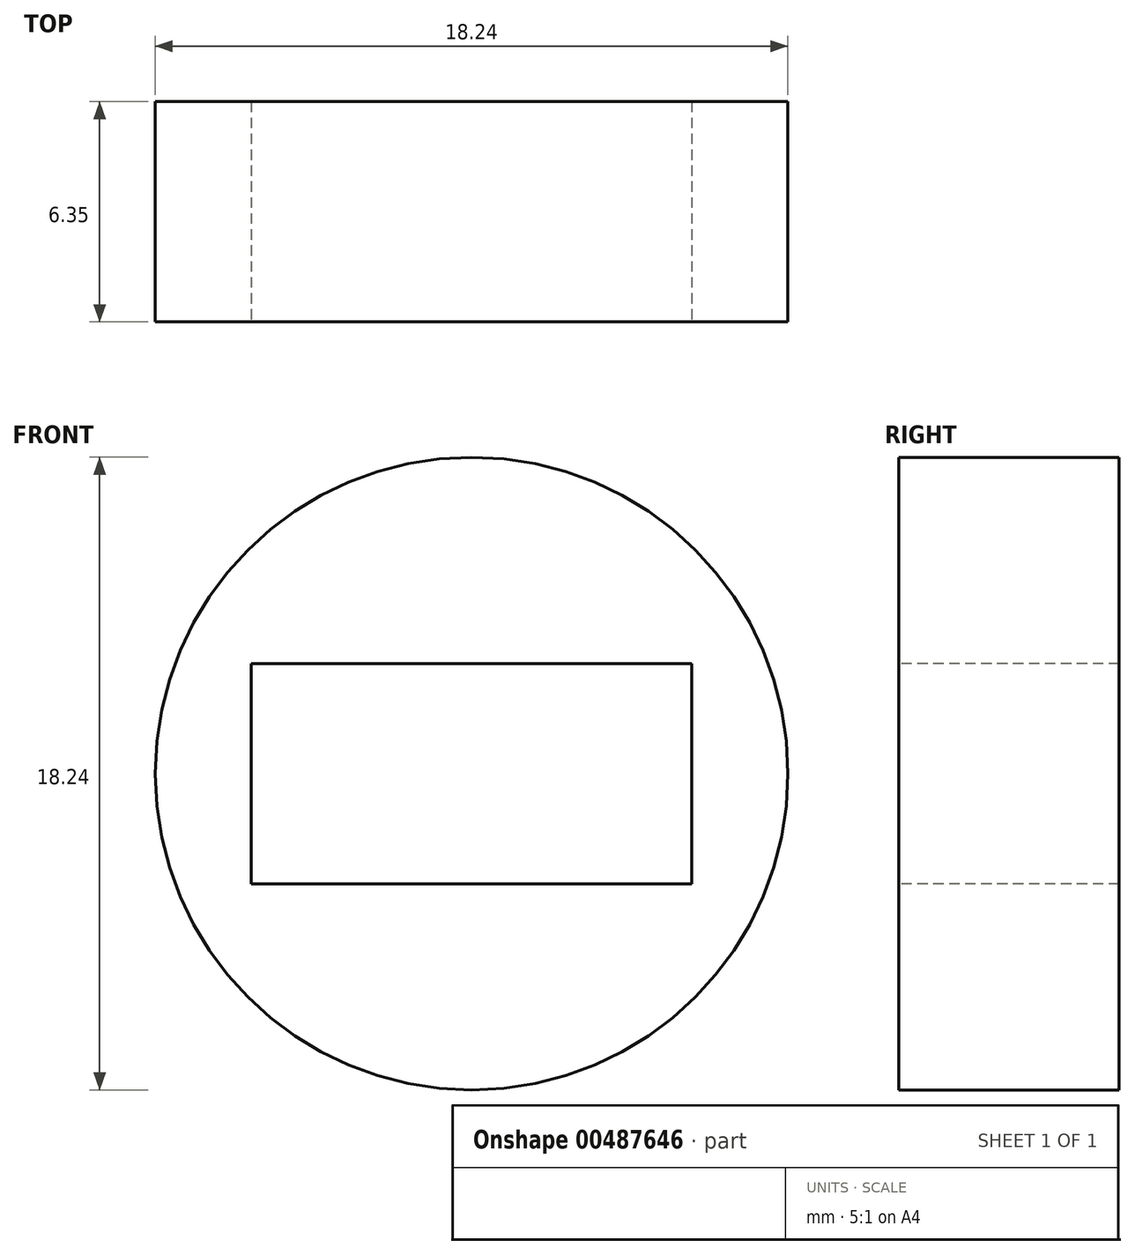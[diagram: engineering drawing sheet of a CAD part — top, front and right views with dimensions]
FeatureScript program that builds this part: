
annotation { "Feature Type Name" : "Feature", "Feature Type Description" : "" }
export const myFeature = defineFeature(function(context is Context, id is Id, definition is map)
    precondition{}
    {
        {
            var Q0;
            Q0=qCreatedBy(makeId("Front.planeOp"),FACE);
            var sketch = newSketch(context, id + "F0", { "sketchPlane" : qUnion([Q0])});
            skCircle(sketch, "E0", {"center": v(0, 0) * mm, "radius": 9.12 * mm});
            skSolve(sketch);
        }
        {
            var Q0;
            Q0 = qSketchRegion(id + "F0", true);
            extrude(context, id + "F1", {"entities" : qUnion([Q0]), "depth" : 6.35 * mm});
        }
        {
            var Q0;
            Q0=makeQuery(id+"F1.opExtrude","CAP_FACE",FACE,{"disambiguationData":[OSD([sQuery(id+"F0.wireOp",EDGE,"E0")])],"isStart":false});
            var sketch = newSketch(context, id + "F2", { "sketchPlane" : qUnion([Q0])});
            skLineSegment(sketch, "E1", {"start": v(-9.12, 0) * mm, "end": v(9.12, 0) * mm, "construction": true});
            skLineSegment(sketch, "E2", {"start": v(-8.55, 3.18) * mm, "end": v(8.55, 3.18) * mm, "construction": true});
            skLineSegment(sketch, "E3", {"start": v(0, 0) * mm, "end": v(0, 4.86) * mm, "construction": true});
            skLineSegment(sketch, "E4", {"start": v(-6.35, 0) * mm, "end": v(-6.35, 4.45) * mm, "construction": true});
            skLineSegment(sketch, "E5.bottom", {"start": v(-6.35, 3.18) * mm, "end": v(6.35, 3.18) * mm});
            skLineSegment(sketch, "E5.top", {"start": v(-6.35, -3.17) * mm, "end": v(6.35, -3.17) * mm});
            skLineSegment(sketch, "E5.left", {"start": v(-6.35, 3.18) * mm, "end": v(-6.35, -3.17) * mm});
            skLineSegment(sketch, "E5.right", {"start": v(6.35, 3.18) * mm, "end": v(6.35, -3.17) * mm});
            skSolve(sketch);
        }
        {
            var Q0;
            Q0 = qSketchRegion(id + "F2", true);
            extrude(context, id + "F3", {"entities" : qUnion([Q0]), "operationType" : NewBodyOperationType.REMOVE, "endBound" : BoundingType.THROUGH_ALL, "oppositeDirection" : true, "depth" : 25.4 * mm});
        }
    });
